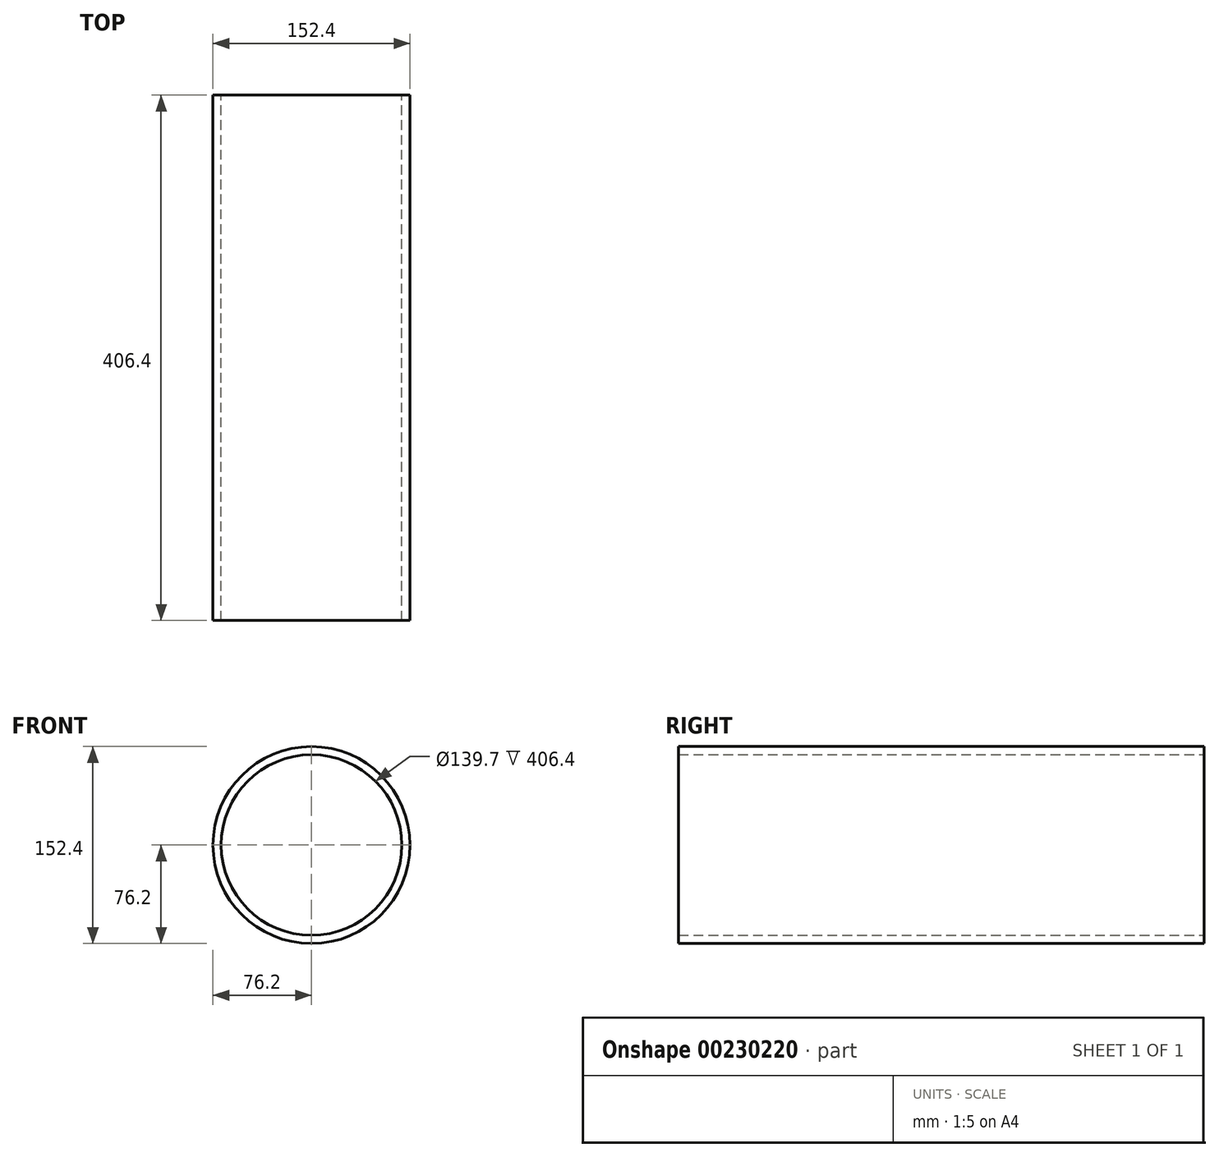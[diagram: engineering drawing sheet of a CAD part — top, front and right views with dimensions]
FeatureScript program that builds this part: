
annotation { "Feature Type Name" : "Feature", "Feature Type Description" : "" }
export const myFeature = defineFeature(function(context is Context, id is Id, definition is map)
    precondition{}
    {
        {
            var Q0;
            Q0=qCreatedBy(makeId("Front.planeOp"),FACE);
            var sketch = newSketch(context, id + "F0", { "sketchPlane" : qUnion([Q0])});
            skCircle(sketch, "E0", {"center": v(0, 0) * mm, "radius": 76.2 * mm});
            skCircle(sketch, "E1", {"center": v(0, 0) * mm, "radius": 69.85 * mm});
            skSolve(sketch);
        }
        {
            var Q0;
            Q0 = qSketchRegion(id + "F0", true);
            extrude(context, id + "F1", {"entities" : qUnion([Q0]), "depth" : 406.4 * mm});
        }
    });
